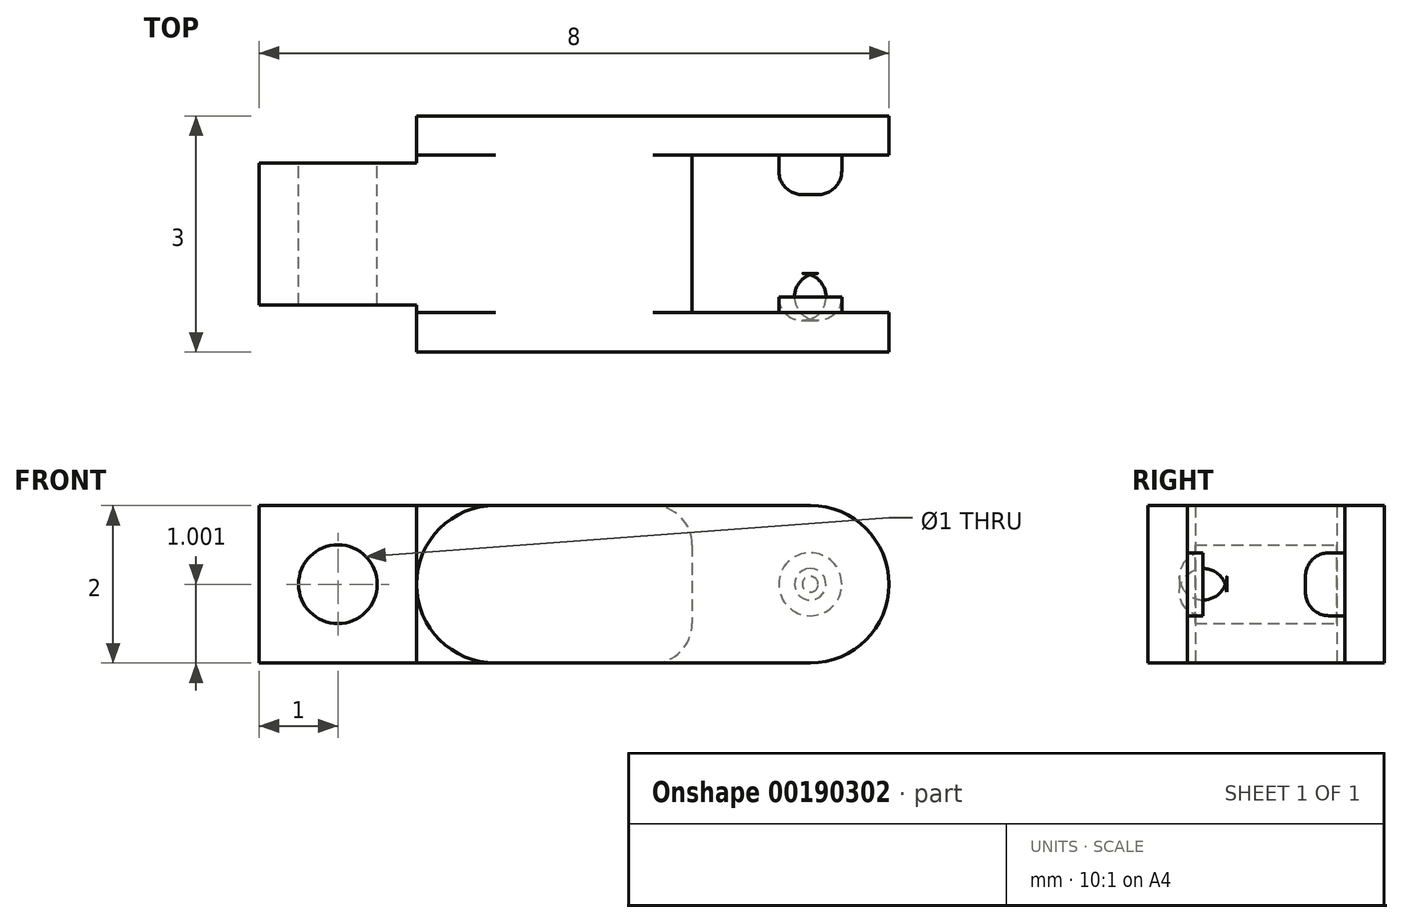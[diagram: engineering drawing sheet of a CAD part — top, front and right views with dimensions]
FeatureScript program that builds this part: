
annotation { "Feature Type Name" : "Feature", "Feature Type Description" : "" }
export const myFeature = defineFeature(function(context is Context, id is Id, definition is map)
    precondition{}
    {
        {
            var Q0;
            Q0=qCreatedBy(makeId("Front.planeOp"),FACE);
            var sketch = newSketch(context, id + "F0", { "sketchPlane" : qUnion([Q0])});
            skLineSegment(sketch, "E0.bottom", {"start": v(-1, -0.25) * mm, "end": v(-7, -0.25) * mm});
            skLineSegment(sketch, "E0.top", {"start": v(-1, -2.25) * mm, "end": v(-7, -2.25) * mm});
            skLineSegment(sketch, "E0.left", {"start": v(-1, -0.25) * mm, "end": v(-1, -2.25) * mm});
            skLineSegment(sketch, "E0.right", {"start": v(-7, -0.25) * mm, "end": v(-7, -2.25) * mm});
            skLineSegment(sketch, "E1", {"start": v(-5, -0.25) * mm, "end": v(-5, -2.25) * mm, "construction": true});
            skArc(sketch, "E2", {"start": v(0, -2.25) * mm, "mid": v(1, -1.25) * mm, "end": v(0, -0.25) * mm});
            skLineSegment(sketch, "E3", {"start": v(-1, -0.25) * mm, "end": v(0, -0.25) * mm});
            skLineSegment(sketch, "E4", {"start": v(-1, -2.25) * mm, "end": v(0, -2.25) * mm});
            skArc(sketch, "E5", {"start": v(-4, -0.25) * mm, "mid": v(-5, -1.25) * mm, "end": v(-4, -2.25) * mm});
            skPoint(sketch, "E6", {"position": v(-6, -1.25) * mm});
            skCircle(sketch, "E7", {"center": v(-6, -1.25) * mm, "radius": 0.5 * mm});
            skCircle(sketch, "E8", {"center": v(0, -1.25) * mm, "radius": 0.4 * mm});
            skCircle(sketch, "E9", {"center": v(0, -1.25) * mm, "radius": 1.41 * mm, "construction": true});
            skLineSegment(sketch, "E10", {"start": v(-1.5, -0.25) * mm, "end": v(-1.5, -1.25) * mm});
            skLineSegment(sketch, "E11", {"start": v(-1.5, -1.25) * mm, "end": v(-1.5, -2.25) * mm});
            skLineSegment(sketch, "E12", {"start": v(0, -0.45) * mm, "end": v(0, -0.25) * mm});
            skSolve(sketch);
        }
        {
            var Q0;
            {var subQ0=sQuery(id+"F0.wireOp",EDGE,"f7VdoiJC-8Tln-2Tbi-K5y5-guD87Exy7ZDr");Q0=makeQuery(id+"F0.imprint","IMPRINT",FACE,{"disambiguationData":[TD([[makeQuery(id+"F0.imprint","IMPRINT",EDGE,{"derivedFrom":subQ0}),-1.0]])]});}
            var Q1;
            {var subQ0=sQuery(id+"F0.wireOp",EDGE,"uH1BQ4Vj-aFWt-8F6M-4EQn-ZlEg98aR2mBw");Q1=makeQuery(id+"F0.imprint","IMPRINT",FACE,{"disambiguationData":[TD([[makeQuery(id+"F0.imprint","IMPRINT",EDGE,{"derivedFrom":subQ0}),1.0]])]});}
            var Q2;
            {var subQ0=sQuery(id+"F0.wireOp",EDGE,"53D6XOHA-X4FV-OfYP-25Ny-iXWlK2nMnlBP");Q2=makeQuery(id+"F0.imprint","IMPRINT",FACE,{"disambiguationData":[TD([[makeQuery(id+"F0.imprint","IMPRINT",EDGE,{"derivedFrom":subQ0}),1.0]])]});}
            var Q3;
            {var subQ3=sQuery(id+"F0.wireOp",EDGE,"mA8XPe0J-LhK4-dBL3-yDRF-5BdcsjTsyDtE");Q3=makeQuery(id+"F0.imprint","IMPRINT",FACE,{"disambiguationData":[TD([[makeQuery(id+"F0.imprint","IMPRINT",EDGE,{"derivedFrom":subQ3}),-1.0]])]});}
            var Q4;
            Q4=makeQuery(id+"F0.imprint","IMPRINT",FACE,{"disambiguationData":[TD([[makeQuery(id+"F0.imprint","IMPRINT",EDGE,{"derivedFrom":sQuery(id+"F0.wireOp",EDGE,"E7")}),1.0]])]});
            var Q5;
            {var subQ6=sQuery(id+"F0.wireOp",EDGE,"E5");Q5=makeQuery(id+"F0.imprint","IMPRINT",FACE,{"disambiguationData":[TD([[makeQuery(id+"F0.imprint","IMPRINT",EDGE,{"derivedFrom":subQ6}),1.0]])]});}
            var Q6;
            {var subQ5=sQuery(id+"F0.wireOp",EDGE,"htJf4tKO-qZep-X4rD-oHbm-76Wo0ydvY8M8.bottom");Q6=makeQuery(id+"F0.imprint","IMPRINT",FACE,{"disambiguationData":[TD([[makeQuery(id+"F0.imprint","IMPRINT",EDGE,{"derivedFrom":subQ5}),-1.0]])]});}
            var Q7;
            {var subQ3=sQuery(id+"F0.wireOp",EDGE,"htJf4tKO-qZep-X4rD-oHbm-76Wo0ydvY8M8.right");Q7=makeQuery(id+"F0.imprint","IMPRINT",FACE,{"disambiguationData":[TD([[makeQuery(id+"F0.imprint","IMPRINT",EDGE,{"derivedFrom":subQ3}),1.0]])]});}
            var Q8;
            {var subQ3=sQuery(id+"F0.wireOp",EDGE,"htJf4tKO-qZep-X4rD-oHbm-76Wo0ydvY8M8.left");Q8=makeQuery(id+"F0.imprint","IMPRINT",FACE,{"disambiguationData":[TD([[makeQuery(id+"F0.imprint","IMPRINT",EDGE,{"derivedFrom":subQ3}),-1.0]])]});}
            var Q9;
            {var subQ1=sQuery(id+"F0.wireOp",EDGE,"E0.right");Q9=makeQuery(id+"F0.imprint","IMPRINT",FACE,{"disambiguationData":[TD([[makeQuery(id+"F0.imprint","IMPRINT",EDGE,{"derivedFrom":subQ1}),1.0]])]});}
            extrude(context, id + "F1", {"entities" : qUnion([Q0, Q1, Q2, Q3, Q4, Q5, Q6, Q7, Q8, Q9]), "depth" : 2 * mm});
        }
        {
            var Q0;
            Q0=makeQuery(id+"F0.imprint","IMPRINT",FACE,{"disambiguationData":[TD([[makeQuery(id+"F0.imprint","IMPRINT",EDGE,{"derivedFrom":sQuery(id+"F0.wireOp",EDGE,"E0.left")}),1.0]])]});
            var Q1;
            {var subQ0=sQuery(id+"F0.wireOp",EDGE,"E0.left");Q1=makeQuery(id+"F0.imprint","IMPRINT",FACE,{"disambiguationData":[TD([[makeQuery(id+"F0.imprint","IMPRINT",EDGE,{"derivedFrom":subQ0}),-1.0]])]});}
            var Q2;
            Q2=makeQuery(id+"F0.imprint","IMPRINT",FACE,{"disambiguationData":[TD([[makeQuery(id+"F0.imprint","IMPRINT",EDGE,{"derivedFrom":sQuery(id+"F0.wireOp",EDGE,"fd2eb06d-ed03-4911-865f-ef9bad8f79ad")}),1.0]])]});
            var Q3;
            {var subQ3=sQuery(id+"F0.wireOp",EDGE,"mA8XPe0J-LhK4-dBL3-yDRF-5BdcsjTsyDtE");Q3=makeQuery(id+"F0.imprint","IMPRINT",FACE,{"disambiguationData":[TD([[makeQuery(id+"F0.imprint","IMPRINT",EDGE,{"derivedFrom":subQ3}),-1.0]])]});}
            var Q4;
            Q4=makeQuery(id+"F0.imprint","IMPRINT",FACE,{"disambiguationData":[TD([[makeQuery(id+"F0.imprint","IMPRINT",EDGE,{"derivedFrom":sQuery(id+"F0.wireOp",EDGE,"E8")}),1.0]])]});
            var Q5;
            {var subQ6=sQuery(id+"F0.wireOp",EDGE,"E5");Q5=makeQuery(id+"F0.imprint","IMPRINT",FACE,{"disambiguationData":[TD([[makeQuery(id+"F0.imprint","IMPRINT",EDGE,{"derivedFrom":subQ6}),1.0]])]});}
            var Q6;
            {var subQ0=sQuery(id+"F0.wireOp",EDGE,"E11");Q6=makeQuery(id+"F0.imprint","IMPRINT",FACE,{"disambiguationData":[TD([[makeQuery(id+"F0.imprint","IMPRINT",EDGE,{"derivedFrom":subQ0}),-1.0]])]});}
            var Q7;
            Q7=makeQuery(id+"F0.imprint","IMPRINT",FACE,{"disambiguationData":[TD([[makeQuery(id+"F0.imprint","IMPRINT",EDGE,{"derivedFrom":sQuery(id+"F0.wireOp",EDGE,"E2")}),1.0]])]});
            var Q8;
            {var subQ0=sQuery(id+"F0.wireOp",EDGE,"E11");Q8=makeQuery(id+"F0.imprint","IMPRINT",FACE,{"disambiguationData":[TD([[makeQuery(id+"F0.imprint","IMPRINT",EDGE,{"derivedFrom":subQ0}),1.0]])]});}
            extrude(context, id + "F2", {"entities" : qUnion([Q0, Q1, Q2, Q3, Q4, Q5, Q6, Q7, Q8]), "operationType" : NewBodyOperationType.ADD, "oppositeDirection" : true, "depth" : 0.5 * mm});
        }
        {
            var Q0;
            Q0=makeQuery(id+"F1.opExtrude","CAP_FACE",FACE,{"disambiguationData":[OSD([sQuery(id+"F0.wireOp",EDGE,"E0.bottom"),sQuery(id+"F0.wireOp",EDGE,"E0.top"),sQuery(id+"F0.wireOp",EDGE,"E0.left"),sQuery(id+"F0.wireOp",EDGE,"E0.right"),sQuery(id+"F0.wireOp",EDGE,"uH1BQ4Vj-aFWt-8F6M-4EQn-ZlEg98aR2mBw"),sQuery(id+"F0.wireOp",EDGE,"kO5BYSIg-LHEv-Mrqp-Hhuf-bGocftPtX9OM"),sQuery(id+"F0.wireOp",EDGE,"f7VdoiJC-8Tln-2Tbi-K5y5-guD87Exy7ZDr"),sQuery(id+"F0.wireOp",EDGE,"Rg8CKrDu-BQip-dAdp-bR6h-5mOOGFjkeTaG")])],"isStart":false});
            var sketch = newSketch(context, id + "F3", { "sketchPlane" : qUnion([Q0])});
            skLineSegment(sketch, "E13", {"start": v(-1, -0.25) * mm, "end": v(-7, -0.25) * mm});
            skArc(sketch, "E14", {"start": v(0, -2.25) * mm, "mid": v(1, -1.25) * mm, "end": v(0, -0.25) * mm});
            skLineSegment(sketch, "E15", {"start": v(-1, -0.25) * mm, "end": v(0, -0.25) * mm});
            skLineSegment(sketch, "E16", {"start": v(-7, -2.25) * mm, "end": v(0, -2.25) * mm});
            skArc(sketch, "E17", {"start": v(-4, -0.25) * mm, "mid": v(-5, -1.25) * mm, "end": v(-4, -2.25) * mm});
            skCircle(sketch, "E18", {"center": v(-6, -1.25) * mm, "radius": 0.5 * mm});
            skCircle(sketch, "E19", {"center": v(0, -1.25) * mm, "radius": 0.4 * mm});
            skSolve(sketch);
        }
        {
            var Q0;
            Q0=makeQuery(id+"F3.imprint","IMPRINT",FACE,{"disambiguationData":[TD([[makeQuery(id+"F3.imprint","IMPRINT",EDGE,{"derivedFrom":sQuery(id+"F3.wireOp",EDGE,"slezlkP0-rkDd-08yD-G4Eu-VJzqF3Z4h6U6")}),1.0]])]});
            var Q1;
            Q1=makeQuery(id+"F3.imprint","IMPRINT",FACE,{"disambiguationData":[TD([[makeQuery(id+"F3.imprint","IMPRINT",EDGE,{"derivedFrom":sQuery(id+"F3.wireOp",EDGE,"slezlkP0-rkDd-08yD-G4Eu-VJzqF3Z4h6U6")}),-1.0]])]});
            var Q2;
            {var subQ0=sQuery(id+"F3.wireOp",EDGE,"E17");Q2=makeQuery(id+"F3.imprint","IMPRINT",FACE,{"disambiguationData":[TD([[makeQuery(id+"F3.imprint","IMPRINT",EDGE,{"derivedFrom":subQ0}),1.0]])]});}
            var Q3;
            Q3=makeQuery(id+"F3.imprint","IMPRINT",FACE,{"disambiguationData":[TD([[makeQuery(id+"F3.imprint","IMPRINT",EDGE,{"derivedFrom":sQuery(id+"F3.wireOp",EDGE,"E14")}),1.0]])]});
            var Q4;
            Q4=makeQuery(id+"F3.imprint","IMPRINT",FACE,{"disambiguationData":[TD([[makeQuery(id+"F3.imprint","IMPRINT",EDGE,{"derivedFrom":sQuery(id+"F3.wireOp",EDGE,"E19")}),1.0]])]});
            var Q5;
            {var subQ1=makeQuery(id+"F1.opExtrude","CAP_EDGE",EDGE,{"disambiguationData":[OSD([sQuery(id+"F0.wireOp",EDGE,"E0.left")])],"isStart":false});Q5=makeQuery(id+"F3.imprint","IMPRINT",FACE,{"disambiguationData":[TD([[makeQuery(id+"F3.imprint","IMPRINT",EDGE,{"derivedFrom":subQ1}),-1.0]])]});}
            extrude(context, id + "F4", {"entities" : qUnion([Q0, Q1, Q2, Q3, Q4, Q5]), "operationType" : NewBodyOperationType.ADD, "depth" : 0.5 * mm});
        }
        {
            var Q0;
            Q0=sQuery(id+"F0.wireOp",VERTEX,"E6");
            var Q1;
            Q1=makeQuery(id+"F1.opExtrude","SWEPT_BODY",BODY,{"disambiguationData":[OSD([sQuery(id+"F0.wireOp",EDGE,"E0.bottom"),sQuery(id+"F0.wireOp",EDGE,"E0.top"),sQuery(id+"F0.wireOp",EDGE,"E0.left"),sQuery(id+"F0.wireOp",EDGE,"E0.right"),sQuery(id+"F0.wireOp",EDGE,"uH1BQ4Vj-aFWt-8F6M-4EQn-ZlEg98aR2mBw"),sQuery(id+"F0.wireOp",EDGE,"kO5BYSIg-LHEv-Mrqp-Hhuf-bGocftPtX9OM"),sQuery(id+"F0.wireOp",EDGE,"f7VdoiJC-8Tln-2Tbi-K5y5-guD87Exy7ZDr"),sQuery(id+"F0.wireOp",EDGE,"Rg8CKrDu-BQip-dAdp-bR6h-5mOOGFjkeTaG"),sQuery(id+"F0.wireOp",EDGE,"mA8XPe0J-LhK4-dBL3-yDRF-5BdcsjTsyDtE")])]});
            hole(context, id + "F5", {"style" : HoleStyle.SIMPLE, "endStyle" : HoleEndStyle.THROUGH, "oppositeDirection" : true, "holeDiameter" : 1 * mm, "locations" : qUnion([Q0]), "scope" : qUnion([Q1]), "isTappedThrough" : true});
        }
        {
            var Q0;
            Q0=makeQuery(id+"F0.imprint","IMPRINT",FACE,{"disambiguationData":[TD([[makeQuery(id+"F0.imprint","IMPRINT",EDGE,{"derivedFrom":sQuery(id+"F0.wireOp",EDGE,"E8")}),1.0]])]});
            extrude(context, id + "F6", {"entities" : qUnion([Q0]), "operationType" : NewBodyOperationType.ADD, "depth" : 0.5 * mm});
        }
        {
            var Q0;
            Q0=makeQuery(id+"F3.imprint","IMPRINT",FACE,{"disambiguationData":[TD([[makeQuery(id+"F3.imprint","IMPRINT",EDGE,{"derivedFrom":sQuery(id+"F3.wireOp",EDGE,"E19")}),1.0]])]});
            extrude(context, id + "F7", {"entities" : qUnion([Q0]), "operationType" : NewBodyOperationType.ADD, "oppositeDirection" : true, "depth" : 0.5 * mm});
        }
        {
            var Q0;
            Q0=makeQuery(id+"F6.opExtrude","CAP_EDGE",EDGE,{"disambiguationData":[OSD([sQuery(id+"F0.wireOp",EDGE,"E8")])],"isStart":false});
            var Q1;
            Q1=makeQuery(id+"F7.opExtrude","CAP_EDGE",EDGE,{"disambiguationData":[OSD([sQuery(id+"F3.wireOp",EDGE,"E19")])],"isStart":false});
            fillet(context, id + "F8", {"entities" : qUnion([Q0, Q1]), "radius" : 0.3 * mm, "tangentPropagation" : true, "allowEdgeOverflow" : false});
        }
        {
            var Q0;
            {var subQ0=sQuery(id+"F0.wireOp",EDGE,"E0.top");Q0=makeQuery(id+"F4.boolean.opBoolean","MERGE",FACE,{"derivedFrom":[makeQuery(id+"F2.boolean.opBoolean","MERGE",FACE,{"derivedFrom":[makeQuery(id+"F1.opExtrude","SWEPT_FACE",FACE,{"disambiguationData":[OSD([subQ0])]}),makeQuery(id+"F2.opExtrude","SWEPT_FACE",FACE,{"disambiguationData":[OSD([subQ0,sQuery(id+"F0.wireOp",EDGE,"E4")])]})]}),makeQuery(id+"F4.opExtrude","SWEPT_FACE",FACE,{"disambiguationData":[OSD([sQuery(id+"F3.wireOp",EDGE,"zInXIRjH-fRHG-3GU0-XYEf-LjIP5AhaiIGm"),sQuery(id+"F3.wireOp",EDGE,"E16")])]})]});}
            var sketch = newSketch(context, id + "F9", { "sketchPlane" : qUnion([Q0])});
            skLineSegment(sketch, "E20.bottom", {"start": v(-5, 2) * mm, "end": v(-7, 2) * mm});
            skLineSegment(sketch, "E20.top", {"start": v(-5, 1.9) * mm, "end": v(-7, 1.9) * mm});
            skLineSegment(sketch, "E20.left", {"start": v(-5, 2) * mm, "end": v(-5, 1.9) * mm});
            skLineSegment(sketch, "E20.right", {"start": v(-7, 2) * mm, "end": v(-7, 1.9) * mm});
            skLineSegment(sketch, "E21.bottom", {"start": v(-5, 0) * mm, "end": v(-7, 0) * mm});
            skLineSegment(sketch, "E21.top", {"start": v(-5, 0.1) * mm, "end": v(-7, 0.1) * mm});
            skLineSegment(sketch, "E21.left", {"start": v(-5, 0) * mm, "end": v(-5, 0.1) * mm});
            skLineSegment(sketch, "E21.right", {"start": v(-7, 0) * mm, "end": v(-7, 0.1) * mm});
            skSolve(sketch);
        }
        {
            var Q0;
            Q0=makeQuery(id+"F9.imprint","IMPRINT",FACE,{"disambiguationData":[TD([[makeQuery(id+"F9.imprint","IMPRINT",EDGE,{"derivedFrom":sQuery(id+"F9.wireOp",EDGE,"E20.bottom")}),1.0]])]});
            var Q1;
            Q1=makeQuery(id+"F9.imprint","IMPRINT",FACE,{"disambiguationData":[TD([[makeQuery(id+"F9.imprint","IMPRINT",EDGE,{"derivedFrom":sQuery(id+"F9.wireOp",EDGE,"E21.bottom")}),-1.0]])]});
            extrude(context, id + "F10", {"entities" : qUnion([Q0, Q1]), "operationType" : NewBodyOperationType.REMOVE, "oppositeDirection" : true, "depth" : 25 * mm});
        }
        {
            var Q0;
            Q0=makeQuery(id+"F10.boolean.opBoolean","COPY",EDGE,{"derivedFrom":makeQuery(id+"F10.opExtrude","SWEPT_EDGE",EDGE,{"disambiguationData":[OSD([sQuery(id+"F0.wireOp",EDGE,"E0.top"),sQuery(id+"F0.wireOp",EDGE,"E0.right"),sQuery(id+"F9.wireOp",EDGE,"E20.top"),sQuery(id+"F9.wireOp",EDGE,"E20.right")])]})});
            var Q1;
            Q1=makeQuery(id+"F10.boolean.opBoolean","COPY",EDGE,{"derivedFrom":makeQuery(id+"F10.opExtrude","SWEPT_EDGE",EDGE,{"disambiguationData":[OSD([sQuery(id+"F0.wireOp",EDGE,"E0.top"),sQuery(id+"F0.wireOp",EDGE,"E0.right"),sQuery(id+"F9.wireOp",EDGE,"E21.top"),sQuery(id+"F9.wireOp",EDGE,"E21.right")])]})});
            var Q2;
            Q2=makeQuery(id+"F1.opExtrude","SWEPT_EDGE",EDGE,{"disambiguationData":[OSD([sQuery(id+"F0.wireOp",EDGE,"E0.bottom"),sQuery(id+"F0.wireOp",EDGE,"E10")])]});
            var Q3;
            Q3=makeQuery(id+"F1.opExtrude","SWEPT_EDGE",EDGE,{"disambiguationData":[OSD([sQuery(id+"F0.wireOp",EDGE,"E0.top"),sQuery(id+"F0.wireOp",EDGE,"E11")])]});
            var Q4;
            Q4=makeQuery(id+"F1.opExtrude","SWEPT_EDGE",EDGE,{"disambiguationData":[OSD([sQuery(id+"F0.wireOp",EDGE,"E10"),sQuery(id+"F0.wireOp",EDGE,"t16F56LC-VUBg-OdEr-BRBj-rz34hXCJSnK6"),sQuery(id+"F0.wireOp",EDGE,"uLMFn6GE-jxci-5nNL-yVyT-isJLdC4N7jqi")])]});
            fillet(context, id + "F11", {"entities" : qUnion([Q0, Q1, Q2, Q3, Q4]), "radius" : .5 * mm, "tangentPropagation" : true, "allowEdgeOverflow" : false});
        }
    });
